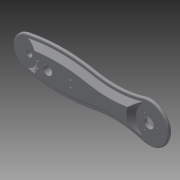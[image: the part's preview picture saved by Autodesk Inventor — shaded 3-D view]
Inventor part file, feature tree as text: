
AUTODESK INVENTOR PART (.ipt)
format: ipt  version: 2015 (Build 190159000, 159)  size: 422,400 bytes
history: native  units: mm
features: sketch x11, extrude x8, fillet x2, chamfer x1
ambient origin geometry x8: Origin, YZ Plane, XZ Plane, XY Plane, X Axis, Y Axis, Z Axis, Center Point
bodies: Solid1 (feature_tree)
feature tree (22):
  extrude  "Extrusion1"  Depth=50.0mm
  extrude  "Extrusion2"  Depth=5.0mm
  extrude  "Extrusion3"  Depth=5.0mm TaperAngle=0.0deg
  extrude  "Extrusion4"  Depth=18.1mm
  extrude  "Extrusion5"  Depth=20.0mm
  extrude  "Extrusion6"  Depth=9.5mm
  sketch  "Sketch7"  dims[d15=9.9mm d16=9.5mm]
  extrude  "Extrusion7"  Depth=9.5mm
  extrude  "Extrusion13"  Depth=3.0mm
  sketch  "Sketch15"  dims[d20=3.0mm]
  chamfer  "Chamfer2"  Distance=13.6mm
  sketch  "Sketch16"  dims[d21=3.0mm d22=13.6mm d23=5.0mm d24=0.0mm d26=2.0mm d29=2.0mm d30=2.0mm d31=5.0mm d32=0.0mm d63=5.0mm d64=0.0mm d65=5.0mm d66=0.0mm d72=20.0mm d73=30.0mm d74=7.3mm d75=0.0mm d103=6.0mm d104=5.0mm d105=0.0mm d106=7.3mm d107=2.0mm d108=45.0deg d109=1.0mm d110=2.0mm]
  fillet  "Fillet1"  Radius=5.0mm
  fillet  "Fillet2"  Radius=2.0mm
  sketch  "Sketch1"  dims[d0=180.0mm d1=50.0mm]
  sketch  "Sketch2"  dims[d2=5.0mm d3=0.0mm d4=15.0mm]
  sketch  "Sketch3"  dims[d5=15.0mm d6=5.0mm d7=0.0mm]
  sketch  "Sketch4"  dims[d9=34.65mm d10=18.1mm]
  sketch  "Sketch5"  dims[d11=55.0mm d12=20.0mm]
  sketch  "Sketch6"  dims[d13=40.2mm d14=9.5mm]
  sketch  "Sketch8"  dims[d17=9.9mm d18=3.0mm]
  sketch  "Sketch14"  dims[d19=3.0mm]
